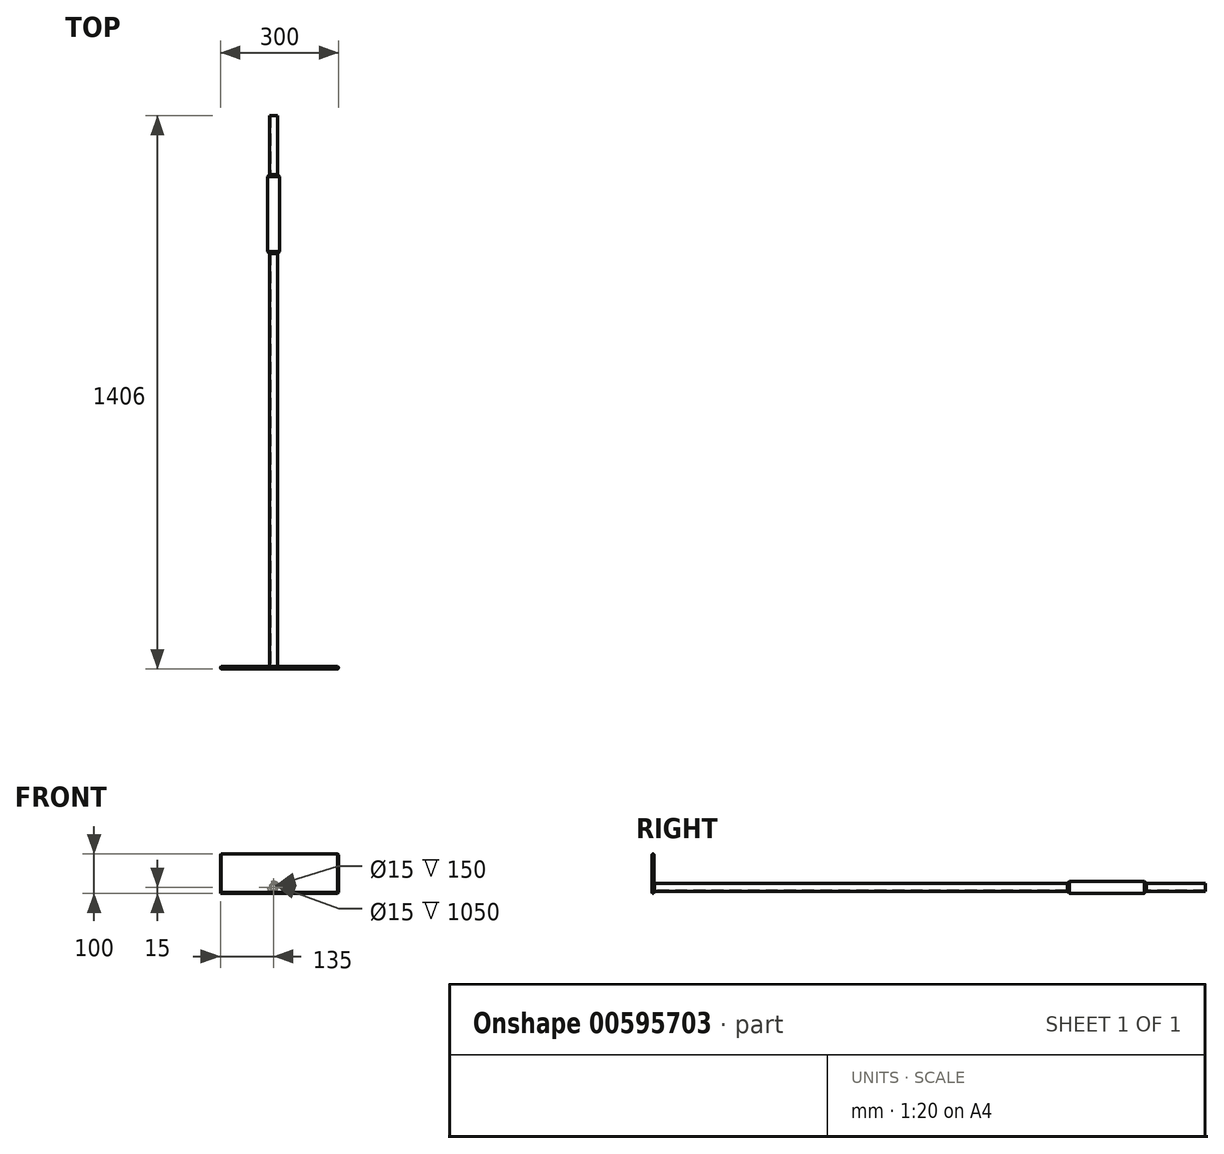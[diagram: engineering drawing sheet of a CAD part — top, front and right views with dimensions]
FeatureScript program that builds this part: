
annotation { "Feature Type Name" : "Feature", "Feature Type Description" : "" }
export const myFeature = defineFeature(function(context is Context, id is Id, definition is map)
    precondition{}
    {
        {
            var Q0;
            Q0=qCreatedBy(makeId("Front.planeOp"),FACE);
            var sketch = newSketch(context, id + "F0", { "sketchPlane" : qUnion([Q0])});
            skCircle(sketch, "E0", {"center": v(0, 0) * mm, "radius": 10 * mm});
            skSolve(sketch);
        }
        {
            var Q0;
            Q0 = qSketchRegion(id + "F0", true);
            var Q1;
            Q1 = qSketchRegion(id + "F2", true);
            extrude(context, id + "F1", {"entities" : qUnion([Q0, Q1]), "oppositeDirection" : true, "depth" : 1406 * mm, "offsetDistance" : 25 * mm});
        }
        {
            var Q0;
            Q0=qCreatedBy(makeId("Front.planeOp"),FACE);
            var sketch = newSketch(context, id + "F2", { "sketchPlane" : qUnion([Q0])});
            skCircle(sketch, "E1", {"center": v(0, 0) * mm, "radius": 7.5 * mm});
            skSolve(sketch);
        }
        {
            var Q0;
            Q0 = qSketchRegion(id + "F2", true);
            extrude(context, id + "F3", {"entities" : qUnion([Q0]), "operationType" : NewBodyOperationType.REMOVE, "oppositeDirection" : true, "depth" : 1800 * mm, "offsetDistance" : 25 * mm});
        }
        {
            var Q0;
            Q0=qCreatedBy(makeId("Right.planeOp"),FACE);
            cPlane(context, id + "F4", {"entities" : qUnion([Q0]), "cplaneType" : CPlaneType.OFFSET, "offset" : 165 * mm, "width" : 150 * mm, "height" : 150 * mm});
        }
        {
            var Q0;
            Q0=qCreatedBy(id+"F4.planeOp",FACE);
            var sketch = newSketch(context, id + "F5", { "sketchPlane" : qUnion([Q0])});
            skLineSegment(sketch, "E2", {"start": v(0, -15) * mm, "end": v(0, 82) * mm});
            skLineSegment(sketch, "E3", {"start": v(0, -15) * mm, "end": v(6, -15) * mm});
            skLineSegment(sketch, "E4", {"start": v(6, -15) * mm, "end": v(6, 82) * mm});
            skArc(sketch, "E5", {"start": v(6, 82) * mm, "mid": v(3, 85) * mm, "end": v(0, 82) * mm});
            skSolve(sketch);
        }
        {
            var Q0;
            Q0 = qSketchRegion(id + "F5", true);
            extrude(context, id + "F6", {"entities" : qUnion([Q0]), "operationType" : NewBodyOperationType.ADD, "oppositeDirection" : true, "depth" : 300 * mm, "offsetDistance" : 25 * mm});
        }
        {
            var Q0;
            Q0=qCreatedBy(makeId("Front.planeOp"),FACE);
            cPlane(context, id + "F7", {"entities" : qUnion([Q0]), "cplaneType" : CPlaneType.OFFSET, "offset" : 1256 * mm, "oppositeDirection" : true, "width" : 150 * mm, "height" : 150 * mm});
        }
        {
            var Q0;
            Q0=qCreatedBy(id+"F7.planeOp",FACE);
            var sketch = newSketch(context, id + "F8", { "sketchPlane" : qUnion([Q0])});
            skCircle(sketch, "E6", {"center": v(0, 0) * mm, "radius": 15 * mm});
            skSolve(sketch);
        }
        {
            var Q0;
            Q0 = qSketchRegion(id + "F8", true);
            extrude(context, id + "F9", {"entities" : qUnion([Q0]), "operationType" : NewBodyOperationType.ADD, "depth" : 200 * mm, "offsetDistance" : 25 * mm});
        }
        {
            var Q0;
            Q0=makeQuery(id+"F9.opExtrude","SWEPT_FACE",FACE,{"disambiguationData":[OSD([sQuery(id+"F8.wireOp",EDGE,"E6")])]});
            chamfer(context, id + "F10", {"entities" : qUnion([Q0]), "width" : 5 * mm, "tangentPropagation" : true});
        }
        {
            var Q0;
            Q0=makeQuery(id+"F6.boolean.opBoolean","INTERSECT",EDGE,{"derivedFrom":[makeQuery(id+"F1.opExtrude","SWEPT_FACE",FACE,{"disambiguationData":[OSD([sQuery(id+"F0.wireOp",EDGE,"E0")])]}),makeQuery(id+"F6.opExtrude","SWEPT_FACE",FACE,{"disambiguationData":[OSD([sQuery(id+"F5.wireOp",EDGE,"E4")])]})]});
            chamfer(context, id + "F11", {"entities" : qUnion([Q0]), "width" : 1 * mm, "tangentPropagation" : true});
        }
        {
            var Q0;
            Q0=makeQuery(id+"F6.opExtrude","CAP_FACE",FACE,{"disambiguationData":[OSD([sQuery(id+"F5.wireOp",EDGE,"E2"),sQuery(id+"F5.wireOp",EDGE,"E3"),sQuery(id+"F5.wireOp",EDGE,"E4"),sQuery(id+"F5.wireOp",EDGE,"E5")])],"isStart":true});
            var Q1;
            Q1=makeQuery(id+"F6.opExtrude","SWEPT_EDGE",EDGE,{"disambiguationData":[OSD([sQuery(id+"F5.wireOp",EDGE,"E2"),sQuery(id+"F5.wireOp",EDGE,"E3")])]});
            var Q2;
            Q2=makeQuery(id+"F6.opExtrude","SWEPT_EDGE",EDGE,{"disambiguationData":[OSD([sQuery(id+"F5.wireOp",EDGE,"E3"),sQuery(id+"F5.wireOp",EDGE,"E4")])]});
            var Q3;
            Q3=makeQuery(id+"F6.opExtrude","SWEPT_EDGE",EDGE,{"disambiguationData":[OSD([sQuery(id+"F5.wireOp",EDGE,"E4"),sQuery(id+"F5.wireOp",EDGE,"E5")])]});
            var Q4;
            Q4=makeQuery(id+"F6.opExtrude","CAP_EDGE",EDGE,{"disambiguationData":[OSD([sQuery(id+"F5.wireOp",EDGE,"E4")])],"isStart":false});
            var Q5;
            Q5=makeQuery(id+"F6.opExtrude","CAP_EDGE",EDGE,{"disambiguationData":[OSD([sQuery(id+"F5.wireOp",EDGE,"E2")])],"isStart":false});
            var Q6;
            Q6=makeQuery(id+"F6.opExtrude","SWEPT_EDGE",EDGE,{"disambiguationData":[OSD([sQuery(id+"F5.wireOp",EDGE,"E2"),sQuery(id+"F5.wireOp",EDGE,"E5")])]});
            var Q7;
            Q7=makeQuery(id+"F6.opExtrude","CAP_EDGE",EDGE,{"disambiguationData":[OSD([sQuery(id+"F5.wireOp",EDGE,"E5")])],"isStart":false});
            chamfer(context, id + "F12", {"entities" : qUnion([Q0, Q1, Q2, Q3, Q4, Q5, Q6, Q7]), "width" : 2 * mm, "tangentPropagation" : true});
        }
    });
